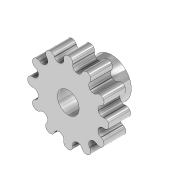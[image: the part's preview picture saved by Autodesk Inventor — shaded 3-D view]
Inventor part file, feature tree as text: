
AUTODESK INVENTOR PART (.ipt)
format: ipt  version: 2020 (Build 240168000, 168)  size: 244,224 bytes
history: native  units: in
note: dims shown in document units (in); Inventor stores cm internally (conversion verified against a paired STEP export)
features: extrude x3, sketch x3
ambient origin geometry x8: Origin, YZ Plane, XZ Plane, XY Plane, X Axis, Y Axis, Z Axis, Center Point
bodies: Solid1 (feature_tree)
feature tree (6):
  extrude  "Extrusion1"  Depth=0.1969in
  extrude  "Extrusion2"  Depth=0.083in
  extrude  "Extrusion3"  Depth=0.1969in
  sketch  "Sketch1"  dims[d0=0.1969in d1=0.563in]
  sketch  "Sketch2"  dims[d2=0.0866in d3=0.083in]
  sketch  "Sketch3"  dims[d4=0.0in d5=0.083in d6=0.083in d7=4.7244in d9=360.0deg d11=0.1969in d12=0.0in d13=0.0787in d14=0.1969in d15=0.0in d16=0.0787in d17=0.1969in d18=0.0in]
